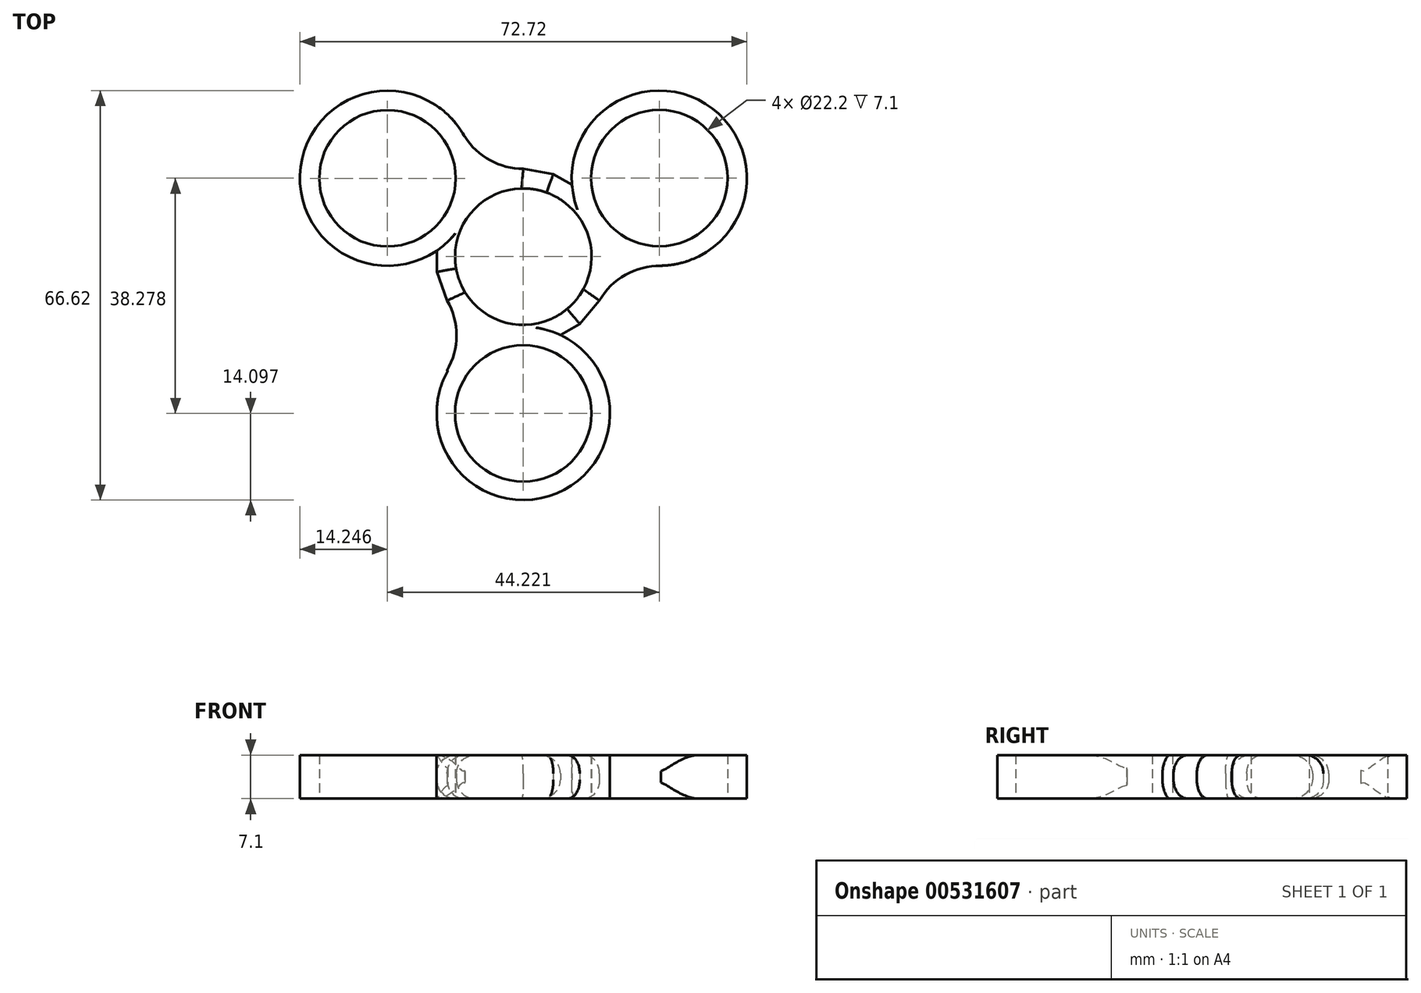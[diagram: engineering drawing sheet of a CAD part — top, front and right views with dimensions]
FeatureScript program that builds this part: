
annotation { "Feature Type Name" : "Feature", "Feature Type Description" : "" }
export const myFeature = defineFeature(function(context is Context, id is Id, definition is map)
    precondition{}
    {
        {
            var Q0;
            Q0=qCreatedBy(makeId("Top.planeOp"),FACE);
            var sketch = newSketch(context, id + "F0", { "sketchPlane" : qUnion([Q0])});
            skCircle(sketch, "E0", {"center": v(0, 0) * mm, "radius": 11.1 * mm});
            skCircle(sketch, "E1.cCircle", {"center": v(0, 0) * mm, "radius": 14.08 * mm, "construction": true});
            skLineSegment(sketch, "E1.0", {"start": v(14.08, 2.48) * mm, "end": v(14.08, -2.48) * mm});
            skLineSegment(sketch, "E1.1", {"start": v(14.08, -2.48) * mm, "end": v(12.38, -7.15) * mm});
            skLineSegment(sketch, "E1.2", {"start": v(12.38, -7.15) * mm, "end": v(9.2, -10.95) * mm});
            skLineSegment(sketch, "E1.3", {"start": v(9.2, -10.95) * mm, "end": v(4.9, -13.44) * mm});
            skLineSegment(sketch, "E1.4", {"start": v(4.9, -13.44) * mm, "end": v(0, -14.3) * mm});
            skLineSegment(sketch, "E1.5", {"start": v(0, -14.3) * mm, "end": v(-4.9, -13.44) * mm});
            skLineSegment(sketch, "E1.6", {"start": v(-4.9, -13.44) * mm, "end": v(-9.2, -10.95) * mm});
            skLineSegment(sketch, "E1.7", {"start": v(-9.2, -10.95) * mm, "end": v(-12.38, -7.15) * mm});
            skLineSegment(sketch, "E1.8", {"start": v(-12.38, -7.15) * mm, "end": v(-14.08, -2.48) * mm});
            skLineSegment(sketch, "E1.9", {"start": v(-14.08, -2.48) * mm, "end": v(-14.08, 2.48) * mm});
            skLineSegment(sketch, "E1.10", {"start": v(-14.08, 2.48) * mm, "end": v(-12.38, 7.15) * mm});
            skLineSegment(sketch, "E1.11", {"start": v(-12.38, 7.15) * mm, "end": v(-9.2, 10.95) * mm});
            skLineSegment(sketch, "E1.12", {"start": v(-9.2, 10.95) * mm, "end": v(-4.9, 13.44) * mm});
            skLineSegment(sketch, "E1.13", {"start": v(-4.9, 13.44) * mm, "end": v(0, 14.3) * mm});
            skLineSegment(sketch, "E1.14", {"start": v(0, 14.3) * mm, "end": v(4.9, 13.44) * mm});
            skLineSegment(sketch, "E1.15", {"start": v(4.9, 13.44) * mm, "end": v(9.2, 10.95) * mm});
            skLineSegment(sketch, "E1.16", {"start": v(9.2, 10.95) * mm, "end": v(12.38, 7.15) * mm});
            skLineSegment(sketch, "E1.17", {"start": v(12.38, 7.15) * mm, "end": v(14.08, 2.48) * mm});
            skPoint(sketch, "E1.0.midPoint", {"position": v(14.08, 0) * mm});
            skLineSegment(sketch, "E2", {"start": v(0, -14.3) * mm, "end": v(0, -25.5) * mm});
            skLineSegment(sketch, "E3", {"start": v(12.38, 7.15) * mm, "end": v(22.13, 12.77) * mm});
            skLineSegment(sketch, "E4", {"start": v(-12.38, 7.15) * mm, "end": v(-22.1, 12.76) * mm});
            skLineSegment(sketch, "E5", {"start": v(0, -25.5) * mm, "end": v(0, -36.25) * mm});
            skLineSegment(sketch, "E6", {"start": v(-22.1, 12.76) * mm, "end": v(-31.44, 18.15) * mm});
            skLineSegment(sketch, "E7", {"start": v(22.13, 12.77) * mm, "end": v(31.92, 18.43) * mm});
            skCircle(sketch, "E8", {"center": v(0, -25.5) * mm, "radius": 11.1 * mm});
            skCircle(sketch, "E9", {"center": v(-22.1, 12.76) * mm, "radius": 11.1 * mm});
            skCircle(sketch, "E10", {"center": v(22.13, 12.77) * mm, "radius": 11.1 * mm});
            skCircle(sketch, "E11.0", {"center": v(-22.1, 12.76) * mm, "radius": 14.25 * mm});
            skCircle(sketch, "E12.0", {"center": v(22.13, 12.77) * mm, "radius": 14.25 * mm});
            skCircle(sketch, "E13.0", {"center": v(0, -25.5) * mm, "radius": 14.1 * mm});
            skLineSegment(sketch, "E14", {"start": v(0, 14.3) * mm, "end": v(0, 25.55) * mm});
            skCircle(sketch, "E15", {"center": v(0, 25.55) * mm, "radius": 11.25 * mm});
            skLineSegment(sketch, "E16", {"start": v(-12.38, -7.15) * mm, "end": v(-22.17, -12.8) * mm});
            skCircle(sketch, "E17", {"center": v(-22.17, -12.8) * mm, "radius": 11.3 * mm});
            skCircle(sketch, "E18", {"center": v(22.17, -12.8) * mm, "radius": 11.3 * mm});
            skCircle(sketch, "E19", {"center": v(15.97, -1.86) * mm, "radius": 6.4 * mm});
            skCircle(sketch, "E20", {"center": v(9.51, -13.38) * mm, "radius": 6.86 * mm});
            skCircle(sketch, "E21", {"center": v(-9.94, -12.85) * mm, "radius": 6.2 * mm});
            skCircle(sketch, "E22", {"center": v(-15.58, -1.28) * mm, "radius": 6.68 * mm});
            skCircle(sketch, "E23", {"center": v(6.28, 14.75) * mm, "radius": 6.3 * mm});
            skPoint(sketch, "E23.second.point", {"position": v(9.78, 20) * mm});
            skPoint(sketch, "E23.third.point", {"position": v(8.83, 9) * mm});
            skCircle(sketch, "E24", {"center": v(-5.99, 14.66) * mm, "radius": 6 * mm});
            skPoint(sketch, "E24.second.point", {"position": v(-9.5, 19.52) * mm});
            skPoint(sketch, "E24.third.point", {"position": v(-8.6, 9.26) * mm});
            skSolve(sketch);
        }
        {
            var Q0;
            {var subQ0=sQuery(id+"F0.wireOp",EDGE,"E20");var subQ1=sQuery(id+"F0.wireOp",EDGE,"E8");var subQ2=makeQuery(id+"F0.imprint","INTERSECT",VERTEX,{"disambiguationData":[OD(1.0)],"derivedFrom":[subQ1,subQ0]});Q0=makeQuery(id+"F0.imprint","IMPRINT",FACE,{"disambiguationData":[TD([[makeQuery(id+"F0.imprint","IMPRINT",EDGE,{"disambiguationData":[TD([[subQ2,1.0]])],"derivedFrom":subQ1}),-1.0]])]});}
            var Q1;
            {var subQ0=sQuery(id+"F0.wireOp",EDGE,"E1.4");var subQ1=sQuery(id+"F0.wireOp",EDGE,"E1.3");var subQ2=makeQuery(id+"F0.imprint","INTERSECT",VERTEX,{"derivedFrom":[subQ1,subQ0]});Q1=makeQuery(id+"F0.imprint","IMPRINT",FACE,{"disambiguationData":[TD([[makeQuery(id+"F0.imprint","IMPRINT",EDGE,{"disambiguationData":[TD([[subQ2,1.0]])],"derivedFrom":subQ1}),1.0]])]});}
            var Q2;
            {var subQ4=sQuery(id+"F0.wireOp",EDGE,"E1.6");var subQ5=sQuery(id+"F0.wireOp",EDGE,"E1.5");var subQ6=makeQuery(id+"F0.imprint","INTERSECT",VERTEX,{"derivedFrom":[subQ5,subQ4]});Q2=makeQuery(id+"F0.imprint","IMPRINT",FACE,{"disambiguationData":[TD([[makeQuery(id+"F0.imprint","IMPRINT",EDGE,{"disambiguationData":[TD([[subQ6,1.0]])],"derivedFrom":subQ5}),1.0]])]});}
            var Q3;
            {var subQ5=sQuery(id+"F0.wireOp",EDGE,"E1.7");Q3=makeQuery(id+"F0.imprint","IMPRINT",FACE,{"disambiguationData":[TD([[makeQuery(id+"F0.imprint","IMPRINT",EDGE,{"derivedFrom":subQ5}),-1.0]])]});}
            var Q4;
            {var subQ9=sQuery(id+"F0.wireOp",EDGE,"E13.0");var subQ11=sQuery(id+"F0.wireOp",EDGE,"E0");var subQ12=makeQuery(id+"F0.imprint","INTERSECT",VERTEX,{"disambiguationData":[OD(0.0)],"derivedFrom":[subQ11,subQ9]});Q4=makeQuery(id+"F0.imprint","IMPRINT",FACE,{"disambiguationData":[TD([[makeQuery(id+"F0.imprint","IMPRINT",EDGE,{"disambiguationData":[TD([[subQ12,-1.0]])],"derivedFrom":subQ11}),-1.0]])]});}
            var Q5;
            {var subQ0=sQuery(id+"F0.wireOp",EDGE,"E1.4");var subQ1=sQuery(id+"F0.wireOp",EDGE,"E1.3");var subQ2=makeQuery(id+"F0.imprint","INTERSECT",VERTEX,{"derivedFrom":[subQ1,subQ0]});Q5=makeQuery(id+"F0.imprint","IMPRINT",FACE,{"disambiguationData":[TD([[makeQuery(id+"F0.imprint","IMPRINT",EDGE,{"disambiguationData":[TD([[subQ2,1.0]])],"derivedFrom":subQ1}),-1.0]])]});}
            var Q6;
            {var subQ0=sQuery(id+"F0.wireOp",EDGE,"E1.6");var subQ1=sQuery(id+"F0.wireOp",EDGE,"E1.5");var subQ2=makeQuery(id+"F0.imprint","INTERSECT",VERTEX,{"derivedFrom":[subQ1,subQ0]});Q6=makeQuery(id+"F0.imprint","IMPRINT",FACE,{"disambiguationData":[TD([[makeQuery(id+"F0.imprint","IMPRINT",EDGE,{"disambiguationData":[TD([[subQ2,1.0]])],"derivedFrom":subQ1}),-1.0]])]});}
            var Q7;
            {var subQ0=sQuery(id+"F0.wireOp",EDGE,"E8");var subQ1=sQuery(id+"F0.wireOp",EDGE,"E1.5");var subQ2=makeQuery(id+"F0.imprint","INTERSECT",VERTEX,{"derivedFrom":[subQ1,subQ0]});Q7=makeQuery(id+"F0.imprint","IMPRINT",FACE,{"disambiguationData":[TD([[makeQuery(id+"F0.imprint","IMPRINT",EDGE,{"disambiguationData":[TD([[subQ2,-1.0]])],"derivedFrom":subQ1}),1.0]])]});}
            var Q8;
            {var subQ0=sQuery(id+"F0.wireOp",EDGE,"E20");var subQ1=sQuery(id+"F0.wireOp",EDGE,"E1.4");var subQ2=makeQuery(id+"F0.imprint","INTERSECT",VERTEX,{"derivedFrom":[subQ1,subQ0]});Q8=makeQuery(id+"F0.imprint","IMPRINT",FACE,{"disambiguationData":[TD([[makeQuery(id+"F0.imprint","IMPRINT",EDGE,{"disambiguationData":[TD([[subQ2,-1.0]])],"derivedFrom":subQ1}),1.0]])]});}
            var Q9;
            {var subQ0=sQuery(id+"F0.wireOp",EDGE,"E13.0");var subQ1=sQuery(id+"F0.wireOp",EDGE,"E0");var subQ2=makeQuery(id+"F0.imprint","INTERSECT",VERTEX,{"disambiguationData":[OD(1.0)],"derivedFrom":[subQ1,subQ0]});Q9=makeQuery(id+"F0.imprint","IMPRINT",FACE,{"disambiguationData":[TD([[makeQuery(id+"F0.imprint","IMPRINT",EDGE,{"disambiguationData":[TD([[subQ2,-1.0]])],"derivedFrom":subQ1}),-1.0]])]});}
            var Q10;
            {var subQ0=sQuery(id+"F0.wireOp",EDGE,"E21");var subQ1=sQuery(id+"F0.wireOp",EDGE,"E0");var subQ2=makeQuery(id+"F0.imprint","INTERSECT",VERTEX,{"disambiguationData":[OD(1.0)],"derivedFrom":[subQ1,subQ0]});Q10=makeQuery(id+"F0.imprint","IMPRINT",FACE,{"disambiguationData":[TD([[makeQuery(id+"F0.imprint","IMPRINT",EDGE,{"disambiguationData":[TD([[subQ2,-1.0]])],"derivedFrom":subQ1}),-1.0]])]});}
            var Q11;
            {var subQ0=sQuery(id+"F0.wireOp",EDGE,"E22");var subQ1=sQuery(id+"F0.wireOp",EDGE,"E0");var subQ2=makeQuery(id+"F0.imprint","INTERSECT",VERTEX,{"disambiguationData":[OD(1.0)],"derivedFrom":[subQ1,subQ0]});Q11=makeQuery(id+"F0.imprint","IMPRINT",FACE,{"disambiguationData":[TD([[makeQuery(id+"F0.imprint","IMPRINT",EDGE,{"disambiguationData":[TD([[subQ2,-1.0]])],"derivedFrom":subQ1}),-1.0]])]});}
            var Q12;
            {var subQ0=sQuery(id+"F0.wireOp",EDGE,"E1.8");Q12=makeQuery(id+"F0.imprint","IMPRINT",FACE,{"disambiguationData":[TD([[makeQuery(id+"F0.imprint","IMPRINT",EDGE,{"derivedFrom":subQ0}),-1.0]])]});}
            var Q13;
            {var subQ0=sQuery(id+"F0.wireOp",EDGE,"E1.10");var subQ1=sQuery(id+"F0.wireOp",EDGE,"E1.9");var subQ2=makeQuery(id+"F0.imprint","INTERSECT",VERTEX,{"derivedFrom":[subQ1,subQ0]});Q13=makeQuery(id+"F0.imprint","IMPRINT",FACE,{"disambiguationData":[TD([[makeQuery(id+"F0.imprint","IMPRINT",EDGE,{"disambiguationData":[TD([[subQ2,1.0]])],"derivedFrom":subQ1}),-1.0]])]});}
            var Q14;
            {var subQ5=sQuery(id+"F0.wireOp",EDGE,"E11.0");var subQ6=sQuery(id+"F0.wireOp",EDGE,"E0");var subQ7=makeQuery(id+"F0.imprint","INTERSECT",VERTEX,{"disambiguationData":[OD(0.0)],"derivedFrom":[subQ6,subQ5]});Q14=makeQuery(id+"F0.imprint","IMPRINT",FACE,{"disambiguationData":[TD([[makeQuery(id+"F0.imprint","IMPRINT",EDGE,{"disambiguationData":[TD([[subQ7,-1.0]])],"derivedFrom":subQ6}),-1.0]])]});}
            var Q15;
            {var subQ0=sQuery(id+"F0.wireOp",EDGE,"E11.0");var subQ1=sQuery(id+"F0.wireOp",EDGE,"E0");var subQ2=makeQuery(id+"F0.imprint","INTERSECT",VERTEX,{"disambiguationData":[OD(1.0)],"derivedFrom":[subQ1,subQ0]});Q15=makeQuery(id+"F0.imprint","IMPRINT",FACE,{"disambiguationData":[TD([[makeQuery(id+"F0.imprint","IMPRINT",EDGE,{"disambiguationData":[TD([[subQ2,-1.0]])],"derivedFrom":subQ1}),-1.0]])]});}
            var Q16;
            {var subQ0=sQuery(id+"F0.wireOp",EDGE,"E9");var subQ1=sQuery(id+"F0.wireOp",EDGE,"E1.11");var subQ2=makeQuery(id+"F0.imprint","INTERSECT",VERTEX,{"derivedFrom":[subQ1,subQ0]});Q16=makeQuery(id+"F0.imprint","IMPRINT",FACE,{"disambiguationData":[TD([[makeQuery(id+"F0.imprint","IMPRINT",EDGE,{"disambiguationData":[TD([[subQ2,-1.0]])],"derivedFrom":subQ1}),1.0]])]});}
            var Q17;
            {var subQ3=sQuery(id+"F0.wireOp",EDGE,"E1.12");var subQ8=sQuery(id+"F0.wireOp",EDGE,"E1.11");var subQ9=makeQuery(id+"F0.imprint","INTERSECT",VERTEX,{"derivedFrom":[subQ8,subQ3]});Q17=makeQuery(id+"F0.imprint","IMPRINT",FACE,{"disambiguationData":[TD([[makeQuery(id+"F0.imprint","IMPRINT",EDGE,{"disambiguationData":[TD([[subQ9,1.0]])],"derivedFrom":subQ8}),1.0]])]});}
            var Q18;
            {var subQ0=sQuery(id+"F0.wireOp",EDGE,"E1.12");var subQ1=sQuery(id+"F0.wireOp",EDGE,"E1.11");var subQ2=makeQuery(id+"F0.imprint","INTERSECT",VERTEX,{"derivedFrom":[subQ1,subQ0]});Q18=makeQuery(id+"F0.imprint","IMPRINT",FACE,{"disambiguationData":[TD([[makeQuery(id+"F0.imprint","IMPRINT",EDGE,{"disambiguationData":[TD([[subQ2,1.0]])],"derivedFrom":subQ1}),-1.0]])]});}
            var Q19;
            {var subQ3=sQuery(id+"F0.wireOp",EDGE,"cm5j0aGU-gvt7-gmux-ldm7-LsrrXDcJTnSL");var subQ9=sQuery(id+"F0.wireOp",EDGE,"E0");var subQ10=makeQuery(id+"F0.imprint","INTERSECT",VERTEX,{"disambiguationData":[OD(1.0)],"derivedFrom":[subQ9,subQ3]});Q19=makeQuery(id+"F0.imprint","IMPRINT",FACE,{"disambiguationData":[TD([[makeQuery(id+"F0.imprint","IMPRINT",EDGE,{"disambiguationData":[TD([[subQ10,-1.0]])],"derivedFrom":subQ9}),-1.0]])]});}
            var Q20;
            {var subQ0=sQuery(id+"F0.wireOp",EDGE,"E22");var subQ1=sQuery(id+"F0.wireOp",EDGE,"E9");var subQ2=makeQuery(id+"F0.imprint","INTERSECT",VERTEX,{"disambiguationData":[OD(0.0)],"derivedFrom":[subQ1,subQ0]});Q20=makeQuery(id+"F0.imprint","IMPRINT",FACE,{"disambiguationData":[TD([[makeQuery(id+"F0.imprint","IMPRINT",EDGE,{"disambiguationData":[TD([[subQ2,1.0]])],"derivedFrom":subQ1}),-1.0]])]});}
            var Q21;
            {var subQ3=sQuery(id+"F0.wireOp",EDGE,"E10");var subQ7=makeQuery(id+"F0.imprint","INTERSECT",VERTEX,{"derivedFrom":[sQuery(id+"F0.wireOp",EDGE,"E7"),subQ3]});Q21=makeQuery(id+"F0.imprint","IMPRINT",FACE,{"disambiguationData":[TD([[makeQuery(id+"F0.imprint","IMPRINT",EDGE,{"disambiguationData":[TD([[subQ7,-1.0]])],"derivedFrom":subQ3}),-1.0]])]});}
            var Q22;
            {var subQ3=sQuery(id+"F0.wireOp",EDGE,"E1.9");var subQ5=sQuery(id+"F0.wireOp",EDGE,"E1.10");var subQ6=makeQuery(id+"F0.imprint","INTERSECT",VERTEX,{"derivedFrom":[subQ3,subQ5]});Q22=makeQuery(id+"F0.imprint","IMPRINT",FACE,{"disambiguationData":[TD([[makeQuery(id+"F0.imprint","IMPRINT",EDGE,{"disambiguationData":[TD([[subQ6,1.0]])],"derivedFrom":subQ3}),1.0]])]});}
            var Q23;
            {var subQ0=sQuery(id+"F0.wireOp",EDGE,"45i7NtGA-5T9x-fNug-wwwZ-XPUVxcpOkaTa");var subQ1=sQuery(id+"F0.wireOp",EDGE,"E0");var subQ2=makeQuery(id+"F0.imprint","INTERSECT",VERTEX,{"disambiguationData":[OD(1.0)],"derivedFrom":[subQ1,subQ0]});Q23=makeQuery(id+"F0.imprint","IMPRINT",FACE,{"disambiguationData":[TD([[makeQuery(id+"F0.imprint","IMPRINT",EDGE,{"disambiguationData":[TD([[subQ2,-1.0]])],"derivedFrom":subQ1}),-1.0]])]});}
            var Q24;
            {var subQ0=sQuery(id+"F0.wireOp",EDGE,"E22");var subQ1=sQuery(id+"F0.wireOp",EDGE,"E1.10");var subQ2=makeQuery(id+"F0.imprint","INTERSECT",VERTEX,{"derivedFrom":[subQ1,subQ0]});Q24=makeQuery(id+"F0.imprint","IMPRINT",FACE,{"disambiguationData":[TD([[makeQuery(id+"F0.imprint","IMPRINT",EDGE,{"disambiguationData":[TD([[subQ2,-1.0]])],"derivedFrom":subQ1}),1.0]])]});}
            var Q25;
            {var subQ4=sQuery(id+"F0.wireOp",EDGE,"E1.16");var subQ5=sQuery(id+"F0.wireOp",EDGE,"E1.15");var subQ6=makeQuery(id+"F0.imprint","INTERSECT",VERTEX,{"derivedFrom":[subQ5,subQ4]});Q25=makeQuery(id+"F0.imprint","IMPRINT",FACE,{"disambiguationData":[TD([[makeQuery(id+"F0.imprint","IMPRINT",EDGE,{"disambiguationData":[TD([[subQ6,1.0]])],"derivedFrom":subQ5}),1.0]])]});}
            var Q26;
            {var subQ3=sQuery(id+"F0.wireOp",EDGE,"cm5j0aGU-gvt7-gmux-ldm7-LsrrXDcJTnSL");var subQ9=sQuery(id+"F0.wireOp",EDGE,"E0");var subQ10=makeQuery(id+"F0.imprint","INTERSECT",VERTEX,{"disambiguationData":[OD(0.0)],"derivedFrom":[subQ9,subQ3]});Q26=makeQuery(id+"F0.imprint","IMPRINT",FACE,{"disambiguationData":[TD([[makeQuery(id+"F0.imprint","IMPRINT",EDGE,{"disambiguationData":[TD([[subQ10,-1.0]])],"derivedFrom":subQ9}),-1.0]])]});}
            var Q27;
            {var subQ3=sQuery(id+"F0.wireOp",EDGE,"45i7NtGA-5T9x-fNug-wwwZ-XPUVxcpOkaTa");var subQ6=sQuery(id+"F0.wireOp",EDGE,"E0");var subQ9=makeQuery(id+"F0.imprint","INTERSECT",VERTEX,{"disambiguationData":[OD(0.0)],"derivedFrom":[subQ6,subQ3]});Q27=makeQuery(id+"F0.imprint","IMPRINT",FACE,{"disambiguationData":[TD([[makeQuery(id+"F0.imprint","IMPRINT",EDGE,{"disambiguationData":[TD([[subQ9,-1.0]])],"derivedFrom":subQ6}),-1.0]])]});}
            var Q28;
            {var subQ1=sQuery(id+"F0.wireOp",EDGE,"E1.13");var subQ3=sQuery(id+"F0.wireOp",EDGE,"cm5j0aGU-gvt7-gmux-ldm7-LsrrXDcJTnSL");var subQ4=makeQuery(id+"F0.imprint","INTERSECT",VERTEX,{"derivedFrom":[subQ1,subQ3]});Q28=makeQuery(id+"F0.imprint","IMPRINT",FACE,{"disambiguationData":[TD([[makeQuery(id+"F0.imprint","IMPRINT",EDGE,{"disambiguationData":[TD([[subQ4,1.0]])],"derivedFrom":subQ3}),1.0]])]});}
            var Q29;
            {var subQ1=sQuery(id+"F0.wireOp",EDGE,"E1.14");var subQ3=sQuery(id+"F0.wireOp",EDGE,"45i7NtGA-5T9x-fNug-wwwZ-XPUVxcpOkaTa");var subQ4=makeQuery(id+"F0.imprint","INTERSECT",VERTEX,{"derivedFrom":[subQ1,subQ3]});Q29=makeQuery(id+"F0.imprint","IMPRINT",FACE,{"disambiguationData":[TD([[makeQuery(id+"F0.imprint","IMPRINT",EDGE,{"disambiguationData":[TD([[subQ4,-1.0]])],"derivedFrom":subQ3}),1.0]])]});}
            var Q30;
            {var subQ0=sQuery(id+"F0.wireOp",EDGE,"cm5j0aGU-gvt7-gmux-ldm7-LsrrXDcJTnSL");var subQ1=sQuery(id+"F0.wireOp",EDGE,"E1.16");var subQ2=makeQuery(id+"F0.imprint","INTERSECT",VERTEX,{"derivedFrom":[subQ1,subQ0]});Q30=makeQuery(id+"F0.imprint","IMPRINT",FACE,{"disambiguationData":[TD([[makeQuery(id+"F0.imprint","IMPRINT",EDGE,{"disambiguationData":[TD([[subQ2,-1.0]])],"derivedFrom":subQ1}),1.0]])]});}
            var Q31;
            {var subQ0=sQuery(id+"F0.wireOp",EDGE,"E12.0");var subQ1=sQuery(id+"F0.wireOp",EDGE,"E0");var subQ2=makeQuery(id+"F0.imprint","INTERSECT",VERTEX,{"disambiguationData":[OD(1.0)],"derivedFrom":[subQ1,subQ0]});Q31=makeQuery(id+"F0.imprint","IMPRINT",FACE,{"disambiguationData":[TD([[makeQuery(id+"F0.imprint","IMPRINT",EDGE,{"disambiguationData":[TD([[subQ2,-1.0]])],"derivedFrom":subQ1}),-1.0]])]});}
            var Q32;
            {var subQ9=sQuery(id+"F0.wireOp",EDGE,"E12.0");var subQ10=sQuery(id+"F0.wireOp",EDGE,"E0");var subQ13=makeQuery(id+"F0.imprint","INTERSECT",VERTEX,{"disambiguationData":[OD(0.0)],"derivedFrom":[subQ10,subQ9]});Q32=makeQuery(id+"F0.imprint","IMPRINT",FACE,{"disambiguationData":[TD([[makeQuery(id+"F0.imprint","IMPRINT",EDGE,{"disambiguationData":[TD([[subQ13,-1.0]])],"derivedFrom":subQ10}),-1.0]])]});}
            var Q33;
            {var subQ0=sQuery(id+"F0.wireOp",EDGE,"E12.0");var subQ1=sQuery(id+"F0.wireOp",EDGE,"E0");var subQ2=makeQuery(id+"F0.imprint","INTERSECT",VERTEX,{"disambiguationData":[OD(0.0)],"derivedFrom":[subQ1,subQ0]});Q33=makeQuery(id+"F0.imprint","IMPRINT",FACE,{"disambiguationData":[TD([[makeQuery(id+"F0.imprint","IMPRINT",EDGE,{"disambiguationData":[TD([[subQ2,1.0]])],"derivedFrom":subQ1}),-1.0]])]});}
            var Q34;
            {var subQ0=sQuery(id+"F0.wireOp",EDGE,"E1.17");var subQ1=sQuery(id+"F0.wireOp",EDGE,"E1.0");var subQ2=makeQuery(id+"F0.imprint","INTERSECT",VERTEX,{"derivedFrom":[subQ1,subQ0]});Q34=makeQuery(id+"F0.imprint","IMPRINT",FACE,{"disambiguationData":[TD([[makeQuery(id+"F0.imprint","IMPRINT",EDGE,{"disambiguationData":[TD([[subQ2,-1.0]])],"derivedFrom":subQ1}),-1.0]])]});}
            var Q35;
            {var subQ5=sQuery(id+"F0.wireOp",EDGE,"E1.1");Q35=makeQuery(id+"F0.imprint","IMPRINT",FACE,{"disambiguationData":[TD([[makeQuery(id+"F0.imprint","IMPRINT",EDGE,{"derivedFrom":subQ5}),-1.0]])]});}
            var Q36;
            {var subQ0=sQuery(id+"F0.wireOp",EDGE,"E20");var subQ1=sQuery(id+"F0.wireOp",EDGE,"E0");var subQ2=makeQuery(id+"F0.imprint","INTERSECT",VERTEX,{"disambiguationData":[OD(1.0)],"derivedFrom":[subQ1,subQ0]});Q36=makeQuery(id+"F0.imprint","IMPRINT",FACE,{"disambiguationData":[TD([[makeQuery(id+"F0.imprint","IMPRINT",EDGE,{"disambiguationData":[TD([[subQ2,-1.0]])],"derivedFrom":subQ1}),-1.0]])]});}
            var Q37;
            {var subQ5=sQuery(id+"F0.wireOp",EDGE,"E1.2");Q37=makeQuery(id+"F0.imprint","IMPRINT",FACE,{"disambiguationData":[TD([[makeQuery(id+"F0.imprint","IMPRINT",EDGE,{"derivedFrom":subQ5}),-1.0]])]});}
            var Q38;
            {var subQ0=sQuery(id+"F0.wireOp",EDGE,"E1.16");var subQ1=sQuery(id+"F0.wireOp",EDGE,"E1.15");var subQ2=makeQuery(id+"F0.imprint","INTERSECT",VERTEX,{"derivedFrom":[subQ1,subQ0]});Q38=makeQuery(id+"F0.imprint","IMPRINT",FACE,{"disambiguationData":[TD([[makeQuery(id+"F0.imprint","IMPRINT",EDGE,{"disambiguationData":[TD([[subQ2,1.0]])],"derivedFrom":subQ1}),-1.0]])]});}
            var Q39;
            {var subQ3=sQuery(id+"F0.wireOp",EDGE,"E1.0");var subQ8=sQuery(id+"F0.wireOp",EDGE,"E1.17");var subQ9=makeQuery(id+"F0.imprint","INTERSECT",VERTEX,{"derivedFrom":[subQ3,subQ8]});Q39=makeQuery(id+"F0.imprint","IMPRINT",FACE,{"disambiguationData":[TD([[makeQuery(id+"F0.imprint","IMPRINT",EDGE,{"disambiguationData":[TD([[subQ9,-1.0]])],"derivedFrom":subQ3}),1.0]])]});}
            var Q40;
            {var subQ0=sQuery(id+"F0.wireOp",EDGE,"E10");var subQ1=sQuery(id+"F0.wireOp",EDGE,"E1.17");var subQ2=makeQuery(id+"F0.imprint","INTERSECT",VERTEX,{"derivedFrom":[subQ1,subQ0]});Q40=makeQuery(id+"F0.imprint","IMPRINT",FACE,{"disambiguationData":[TD([[makeQuery(id+"F0.imprint","IMPRINT",EDGE,{"disambiguationData":[TD([[subQ2,-1.0]])],"derivedFrom":subQ1}),1.0]])]});}
            var Q41;
            {var subQ2=sQuery(id+"F0.wireOp",EDGE,"E1.1");Q41=makeQuery(id+"F0.imprint","IMPRINT",FACE,{"disambiguationData":[TD([[makeQuery(id+"F0.imprint","IMPRINT",EDGE,{"derivedFrom":subQ2}),1.0]])]});}
            var Q42;
            {var subQ3=sQuery(id+"F0.wireOp",EDGE,"E1.12");var subQ7=sQuery(id+"F0.wireOp",EDGE,"E1.13");var subQ8=makeQuery(id+"F0.imprint","INTERSECT",VERTEX,{"derivedFrom":[subQ3,subQ7]});Q42=makeQuery(id+"F0.imprint","IMPRINT",FACE,{"disambiguationData":[TD([[makeQuery(id+"F0.imprint","IMPRINT",EDGE,{"disambiguationData":[TD([[subQ8,1.0]])],"derivedFrom":subQ3}),1.0]])]});}
            var Q43;
            {var subQ5=sQuery(id+"F0.wireOp",EDGE,"E1.7");Q43=makeQuery(id+"F0.imprint","IMPRINT",FACE,{"disambiguationData":[TD([[makeQuery(id+"F0.imprint","IMPRINT",EDGE,{"derivedFrom":subQ5}),1.0]])]});}
            var Q44;
            {var subQ5=sQuery(id+"F0.wireOp",EDGE,"E1.14");Q44=makeQuery(id+"F0.imprint","IMPRINT",FACE,{"disambiguationData":[TD([[makeQuery(id+"F0.imprint","IMPRINT",EDGE,{"derivedFrom":subQ5}),-1.0]])]});}
            var Q45;
            {var subQ5=sQuery(id+"F0.wireOp",EDGE,"E1.13");Q45=makeQuery(id+"F0.imprint","IMPRINT",FACE,{"disambiguationData":[TD([[makeQuery(id+"F0.imprint","IMPRINT",EDGE,{"derivedFrom":subQ5}),-1.0]])]});}
            var Q46;
            {var subQ0=sQuery(id+"F0.wireOp",EDGE,"E23");var subQ1=sQuery(id+"F0.wireOp",EDGE,"E0");var subQ2=makeQuery(id+"F0.imprint","INTERSECT",VERTEX,{"disambiguationData":[OD(1.0)],"derivedFrom":[subQ1,subQ0]});Q46=makeQuery(id+"F0.imprint","IMPRINT",FACE,{"disambiguationData":[TD([[makeQuery(id+"F0.imprint","IMPRINT",EDGE,{"disambiguationData":[TD([[subQ2,-1.0]])],"derivedFrom":subQ1}),-1.0]])]});}
            var Q47;
            {var subQ0=sQuery(id+"F0.wireOp",EDGE,"E24");var subQ1=sQuery(id+"F0.wireOp",EDGE,"E0");var subQ2=makeQuery(id+"F0.imprint","INTERSECT",VERTEX,{"disambiguationData":[OD(1.0)],"derivedFrom":[subQ1,subQ0]});Q47=makeQuery(id+"F0.imprint","IMPRINT",FACE,{"disambiguationData":[TD([[makeQuery(id+"F0.imprint","IMPRINT",EDGE,{"disambiguationData":[TD([[subQ2,-1.0]])],"derivedFrom":subQ1}),-1.0]])]});}
            var Q48;
            {var subQ0=sQuery(id+"F0.wireOp",EDGE,"E4");var subQ5=sQuery(id+"F0.wireOp",EDGE,"E9");var subQ6=makeQuery(id+"F0.imprint","INTERSECT",VERTEX,{"derivedFrom":[subQ0,subQ5]});Q48=makeQuery(id+"F0.imprint","IMPRINT",FACE,{"disambiguationData":[TD([[makeQuery(id+"F0.imprint","IMPRINT",EDGE,{"disambiguationData":[TD([[subQ6,-1.0]])],"derivedFrom":subQ5}),-1.0]])]});}
            var Q49;
            {var subQ0=sQuery(id+"F0.wireOp",EDGE,"E22");var subQ1=sQuery(id+"F0.wireOp",EDGE,"E11.0");var subQ2=makeQuery(id+"F0.imprint","INTERSECT",VERTEX,{"disambiguationData":[OD(1.0)],"derivedFrom":[subQ1,subQ0]});Q49=makeQuery(id+"F0.imprint","IMPRINT",FACE,{"disambiguationData":[TD([[makeQuery(id+"F0.imprint","IMPRINT",EDGE,{"disambiguationData":[TD([[subQ2,-1.0]])],"derivedFrom":subQ1}),1.0]])]});}
            var Q50;
            {var subQ3=sQuery(id+"F0.wireOp",EDGE,"E12.0");var subQ5=sQuery(id+"F0.wireOp",EDGE,"E23");var subQ6=makeQuery(id+"F0.imprint","INTERSECT",VERTEX,{"disambiguationData":[OD(1.0)],"derivedFrom":[subQ3,subQ5]});Q50=makeQuery(id+"F0.imprint","IMPRINT",FACE,{"disambiguationData":[TD([[makeQuery(id+"F0.imprint","IMPRINT",EDGE,{"disambiguationData":[TD([[subQ6,-1.0]])],"derivedFrom":subQ3}),1.0]])]});}
            var Q51;
            {var subQ0=sQuery(id+"F0.wireOp",EDGE,"E23");var subQ1=sQuery(id+"F0.wireOp",EDGE,"E0");var subQ2=makeQuery(id+"F0.imprint","INTERSECT",VERTEX,{"disambiguationData":[OD(0.0)],"derivedFrom":[subQ1,subQ0]});Q51=makeQuery(id+"F0.imprint","IMPRINT",FACE,{"disambiguationData":[TD([[makeQuery(id+"F0.imprint","IMPRINT",EDGE,{"disambiguationData":[TD([[subQ2,1.0]])],"derivedFrom":subQ1}),-1.0]])]});}
            var Q52;
            {var subQ0=sQuery(id+"F0.wireOp",EDGE,"E3");var subQ5=sQuery(id+"F0.wireOp",EDGE,"E10");var subQ6=makeQuery(id+"F0.imprint","INTERSECT",VERTEX,{"derivedFrom":[subQ0,subQ5]});Q52=makeQuery(id+"F0.imprint","IMPRINT",FACE,{"disambiguationData":[TD([[makeQuery(id+"F0.imprint","IMPRINT",EDGE,{"disambiguationData":[TD([[subQ6,-1.0]])],"derivedFrom":subQ5}),-1.0]])]});}
            var Q53;
            {var subQ0=sQuery(id+"F0.wireOp",EDGE,"E20");var subQ3=sQuery(id+"F0.wireOp",EDGE,"E13.0");var subQ4=makeQuery(id+"F0.imprint","INTERSECT",VERTEX,{"disambiguationData":[OD(1.0)],"derivedFrom":[subQ3,subQ0]});Q53=makeQuery(id+"F0.imprint","IMPRINT",FACE,{"disambiguationData":[TD([[makeQuery(id+"F0.imprint","IMPRINT",EDGE,{"disambiguationData":[TD([[subQ4,-1.0]])],"derivedFrom":subQ3}),1.0]])]});}
            var Q54;
            {var subQ0=sQuery(id+"F0.wireOp",EDGE,"E2");var subQ5=sQuery(id+"F0.wireOp",EDGE,"E8");var subQ6=makeQuery(id+"F0.imprint","INTERSECT",VERTEX,{"derivedFrom":[subQ0,subQ5]});Q54=makeQuery(id+"F0.imprint","IMPRINT",FACE,{"disambiguationData":[TD([[makeQuery(id+"F0.imprint","IMPRINT",EDGE,{"disambiguationData":[TD([[subQ6,-1.0]])],"derivedFrom":subQ5}),-1.0]])]});}
            extrude(context, id + "F1", {"entities" : qUnion([Q0, Q1, Q2, Q3, Q4, Q5, Q6, Q7, Q8, Q9, Q10, Q11, Q12, Q13, Q14, Q15, Q16, Q17, Q18, Q19, Q20, Q21, Q22, Q23, Q24, Q25, Q26, Q27, Q28, Q29, Q30, Q31, Q32, Q33, Q34, Q35, Q36, Q37, Q38, Q39, Q40, Q41, Q42, Q43, Q44, Q45, Q46, Q47, Q48, Q49, Q50, Q51, Q52, Q53, Q54]), "depth" : 7.1 * mm, "offsetDistance" : 25 * mm});
        }
        {
            var Q0;
            Q0=makeQuery(id+"F1.opExtrude","CAP_EDGE",EDGE,{"disambiguationData":[OSD([sQuery(id+"F0.wireOp",EDGE,"E1.15")])],"isStart":false});
            var Q1;
            Q1=makeQuery(id+"F1.opExtrude","CAP_EDGE",EDGE,{"disambiguationData":[OSD([sQuery(id+"F0.wireOp",EDGE,"E1.14")])],"isStart":false});
            var Q2;
            Q2=makeQuery(id+"F1.opExtrude","CAP_EDGE",EDGE,{"disambiguationData":[OSD([sQuery(id+"F0.wireOp",EDGE,"E15")])],"isStart":false});
            var Q3;
            Q3=makeQuery(id+"F1.opExtrude","CAP_EDGE",EDGE,{"disambiguationData":[OSD([sQuery(id+"F0.wireOp",EDGE,"E18")])],"isStart":false});
            var Q4;
            Q4=makeQuery(id+"F1.opExtrude","CAP_EDGE",EDGE,{"disambiguationData":[OSD([sQuery(id+"F0.wireOp",EDGE,"E1.9")])],"isStart":false});
            var Q5;
            Q5=makeQuery(id+"F1.opExtrude","CAP_EDGE",EDGE,{"disambiguationData":[OSD([sQuery(id+"F0.wireOp",EDGE,"E1.8")])],"isStart":false});
            var Q6;
            Q6=makeQuery(id+"F1.opExtrude","CAP_EDGE",EDGE,{"disambiguationData":[OSD([sQuery(id+"F0.wireOp",EDGE,"E17")])],"isStart":false});
            var Q7;
            Q7=makeQuery(id+"F1.opExtrude","CAP_EDGE",EDGE,{"disambiguationData":[OSD([sQuery(id+"F0.wireOp",EDGE,"E1.3")])],"isStart":false});
            var Q8;
            Q8=makeQuery(id+"F1.opExtrude","CAP_EDGE",EDGE,{"disambiguationData":[OSD([sQuery(id+"F0.wireOp",EDGE,"E1.2")])],"isStart":false});
            var Q9;
            Q9=makeQuery(id+"F1.opExtrude","CAP_EDGE",EDGE,{"disambiguationData":[OSD([sQuery(id+"F0.wireOp",EDGE,"E17")])],"isStart":true});
            var Q10;
            Q10=makeQuery(id+"F1.opExtrude","CAP_EDGE",EDGE,{"disambiguationData":[OSD([sQuery(id+"F0.wireOp",EDGE,"E1.8")])],"isStart":true});
            var Q11;
            Q11=makeQuery(id+"F1.opExtrude","CAP_EDGE",EDGE,{"disambiguationData":[OSD([sQuery(id+"F0.wireOp",EDGE,"E1.9")])],"isStart":true});
            var Q12;
            Q12=makeQuery(id+"F1.opExtrude","CAP_EDGE",EDGE,{"disambiguationData":[OSD([sQuery(id+"F0.wireOp",EDGE,"E1.3")])],"isStart":true});
            var Q13;
            Q13=makeQuery(id+"F1.opExtrude","CAP_EDGE",EDGE,{"disambiguationData":[OSD([sQuery(id+"F0.wireOp",EDGE,"E1.2")])],"isStart":true});
            var Q14;
            Q14=makeQuery(id+"F1.opExtrude","CAP_EDGE",EDGE,{"disambiguationData":[OSD([sQuery(id+"F0.wireOp",EDGE,"E18")])],"isStart":true});
            var Q15;
            Q15=makeQuery(id+"F1.opExtrude","CAP_EDGE",EDGE,{"disambiguationData":[OSD([sQuery(id+"F0.wireOp",EDGE,"E1.15")])],"isStart":true});
            var Q16;
            Q16=makeQuery(id+"F1.opExtrude","CAP_EDGE",EDGE,{"disambiguationData":[OSD([sQuery(id+"F0.wireOp",EDGE,"E15")])],"isStart":true});
            var Q17;
            Q17=makeQuery(id+"F1.opExtrude","CAP_EDGE",EDGE,{"disambiguationData":[OSD([sQuery(id+"F0.wireOp",EDGE,"E1.14")])],"isStart":true});
            fillet(context, id + "F2", {"entities" : qUnion([Q0, Q1, Q2, Q3, Q4, Q5, Q6, Q7, Q8, Q9, Q10, Q11, Q12, Q13, Q14, Q15, Q16, Q17]), "radius" : 3.04 * mm, "tangentPropagation" : true, "allowEdgeOverflow" : false});
        }
    });
